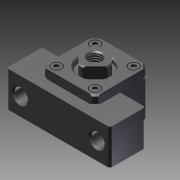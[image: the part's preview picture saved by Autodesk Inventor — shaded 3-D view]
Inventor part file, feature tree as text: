
AUTODESK INVENTOR PART (.ipt)
format: ipt  version: 2016 (Build 200138000, 138)  size: 366,080 bytes
history: native  units: mm
features: sketch x23, revolve x14, other x14, extrude x8, pattern_linear x3, thread x1, hole x1
ambient origin geometry x8: Origin, YZ Plane, XZ Plane, XY Plane, X Axis, Y Axis, Z Axis, Center Point
bodies: Solid1 (feature_tree)
feature tree (64):
  extrude  "Extrusion1"  TaperAngle=360.0deg  [1 undecoded]
  revolve  "Revolution1"  [1 undecoded]
  revolve  "Revolution2"  [1 undecoded]
  extrude  "Extrusion2"  TaperAngle=360.0deg  [1 undecoded]
  revolve  "Revolution3"  [1 undecoded]
  extrude  "Extrusion3"  TaperAngle=360.0deg  [1 undecoded]
  extrude  "Extrusion4"  Depth=20.0mm
  revolve  "Revolution4"  [1 undecoded]
  revolve  "Revolution5"  Angle=360.0deg
  thread  "Thread1"  [1 undecoded]
  revolve  "Revolution6"  [1 undecoded]
  revolve  "Revolution7"  Angle=360.0deg
  extrude  "Extrusion5"  TaperAngle=360.0deg  [1 undecoded]
  pattern_linear  "Rectangular Pattern1"  [2 undecoded]
  pattern_linear  "Rectangular Pattern2"  [2 undecoded]
  pattern_linear  "Rectangular Pattern3"  [2 undecoded]
  revolve  "Revolution8"  [1 undecoded]
  revolve  "Revolution9"  [1 undecoded]
  revolve  "Revolution10"  [1 undecoded]
  revolve  "Revolution11"  [1 undecoded]
  extrude  "Extrusion6"  [1 undecoded]
  hole  "Hole1"  [1 undecoded]
  revolve  "Revolution12"  [1 undecoded]
  extrude  "Extrusion7"  [1 undecoded]
  revolve  "Revolution13"  [1 undecoded]
  revolve  "Revolution14"  [1 undecoded]
  extrude  "Extrusion8"  [1 undecoded]
  other  "unit_XY"
  other  "unit_YZ"
  other  "unit_ZX"
  other  "unit_X"
  other  "unit_Y"
  other  "unit_Z"
  other  "unit_Center"
  other  "unit_collar_XY"
  other  "unit_collar_YZ"
  other  "unit_collar_ZX"
  other  "unit_collar_X"
  other  "unit_collar_Y"
  other  "unit_collar_Z"
  other  "unit_collar_Center"
  sketch  "Sketch_1"  dims[d0=24.0mm d1=0.0mm d2=360.0deg]
  sketch  "Sketch_3"  dims[d3=360.0deg d4=3.0mm d5=0.0mm]
  sketch  "Sketch_4"  dims[d6=360.0deg d7=8.5mm d8=0.0mm]
  sketch  "Sketch_17"  dims[d12=360.0deg d13=6.376mm d14=0.0mm]
  sketch  "Sketch_19"  dims[d25=20.0mm d27=26.162951mm d28=20.0mm d30=26.162951mm d31=20.0mm d33=26.162951mm d34=20.0mm d36=26.162951mm]
  sketch  "Sketch_18"  dims[d15=360.0deg d16=360.0deg]
  sketch  "Sketch_20"  dims[d37=360.0deg d38=360.0deg d39=360.0deg]
  sketch  "Sketch_21"  dims[d40=360.0deg d41=1.2mm d42=0.0mm]
  sketch  "Sketch_22"  dims[d43=10.0mm d44=6.0mm d45=14.5mm d46=6.0mm d47=90.0deg d48=27.5mm d49=0.0mm d50=360.0deg]
  sketch  "Sketch_24"  dims[d51=6.0mm d52=0.0mm d53=360.0deg]
  sketch  "Sketch_25"  dims[d54=360.0deg]
  sketch  "Sketch_28"  dims[d55=0.01mm d56=0.0mm]
  sketch  "Sketch_30"  dims[d57=0.0mm d58=0.0mm]
  sketch  "Sketch_31"
  sketch  "Sketch_32"
  sketch  "Sketch_33"
  sketch  "Sketch_34"
  sketch  "Sketch18"  dims[d17=3.0mm d18=0.0mm d19=20.0mm d21=26.162951mm d22=20.0mm d24=26.162951mm]
  sketch  "Sketch_55"
  sketch  "Sketch_16"  dims[d9=3.0mm d10=0.0mm d11=360.0deg]
  sketch  "Sketch_35"
  sketch  "Sketch_50"
  sketch  "Sketch_51"
note: 27 required parameter values undecoded (feature->parameter linkage not recoverable at this tier; creation-order binding heuristic only, values carry confidence <= 0.55)